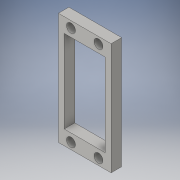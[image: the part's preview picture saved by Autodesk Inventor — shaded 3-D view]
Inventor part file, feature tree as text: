
AUTODESK INVENTOR PART (.ipt)
format: ipt  version: 2016 (Build 200138000, 138)  size: 103,424 bytes
history: native  units: in
note: dims shown in document units (in); Inventor stores cm internally (conversion verified against a paired STEP export)
features: extrude x1, sketch x1
ambient origin geometry x8: Origin, YZ Plane, XZ Plane, XY Plane, X Axis, Y Axis, Z Axis, Center Point
bodies: Solid1 (feature_tree)
feature tree (2):
  extrude  "Extrusion1"  Depth=2.12in
  sketch  "Sketch1"  dims[d0=1.0in d1=2.12in d3=1.57in d4=0.2in d5=0.0in]
